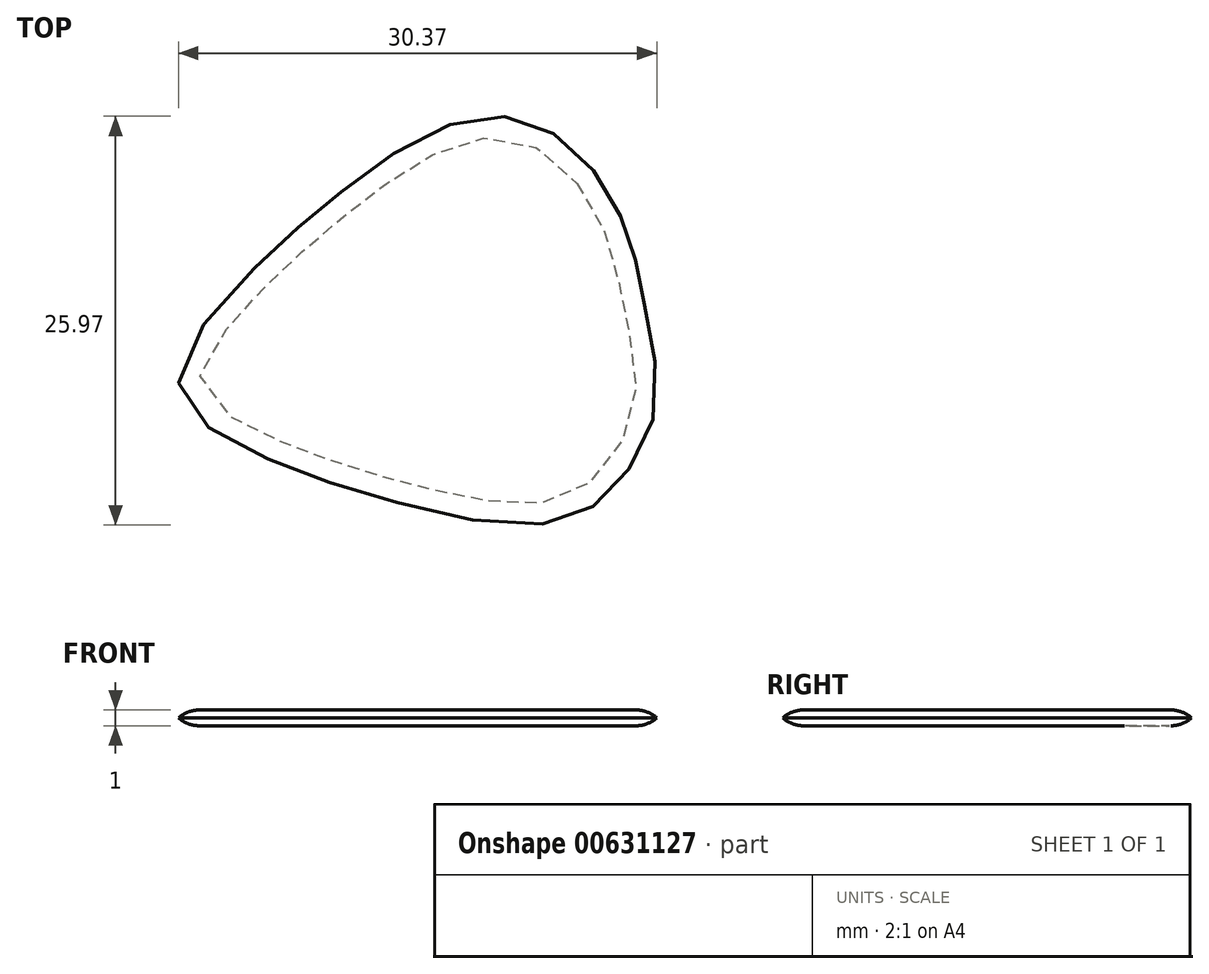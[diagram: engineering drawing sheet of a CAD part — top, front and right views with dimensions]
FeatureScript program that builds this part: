
annotation { "Feature Type Name" : "Feature", "Feature Type Description" : "" }
export const myFeature = defineFeature(function(context is Context, id is Id, definition is map)
    precondition{}
    {
        {
            var Q0;
            Q0=qCreatedBy(makeId("Top.planeOp"),FACE);
            var sketch = newSketch(context, id + "F0", { "sketchPlane" : qUnion([Q0])});
            skFitSpline(sketch, "E0", {"points": [v(27.37, -5.39) * mm, v(23, -2.2) * mm, v(17.33, -2.85) * mm, v(10.68, -7.28) * mm, v(5.98, -11.45) * mm, v(1.03, -19.01) * mm, v(5.98, -23.38) * mm, v(14.33, -26.32) * mm, v(24.5, -27.82) * mm, v(28.93, -25.27) * mm, v(31.34, -20.06) * mm, v(30.56, -13.73) * mm, v(29.71, -9.89) * mm, v(27.37, -5.39) * mm]});
            skSolve(sketch);
        }
        {
            var Q0;
            Q0=makeQuery(id+"F0.imprint","IMPRINT",FACE,{"disambiguationData":[TD([[makeQuery(id+"F0.imprint","IMPRINT",EDGE,{"derivedFrom":sQuery(id+"F0.wireOp",EDGE,"E0")}),1.0]])]});
            extrude(context, id + "F1", {"entities" : qUnion([Q0]), "depth" : 0.5 * mm});
        }
        {
            var Q0;
            Q0=makeQuery(id+"F1.opExtrude","CAP_EDGE",EDGE,{"disambiguationData":[OSD([sQuery(id+"F0.wireOp",EDGE,"E0")])],"isStart":false});
            fillet(context, id + "F2", {"entities" : qUnion([Q0]), "radius" : 2 * mm, "tangentPropagation" : true, "allowEdgeOverflow" : false});
        }
        {
            var Q0;
            Q0=makeQuery(id+"F1.opExtrude","CAP_FACE",FACE,{"disambiguationData":[OSD([sQuery(id+"F0.wireOp",EDGE,"E0")])],"isStart":true});
            extrude(context, id + "F3", {"entities" : qUnion([Q0]), "depth" : 0.5 * mm});
        }
        {
            var Q0;
            Q0=makeQuery(id+"F3.opExtrude","CAP_EDGE",EDGE,{"disambiguationData":[OSD([sQuery(id+"F0.wireOp",EDGE,"E0")])],"isStart":false});
            fillet(context, id + "F4", {"entities" : qUnion([Q0]), "radius" : 2 * mm, "tangentPropagation" : true, "allowEdgeOverflow" : false});
        }
    });
